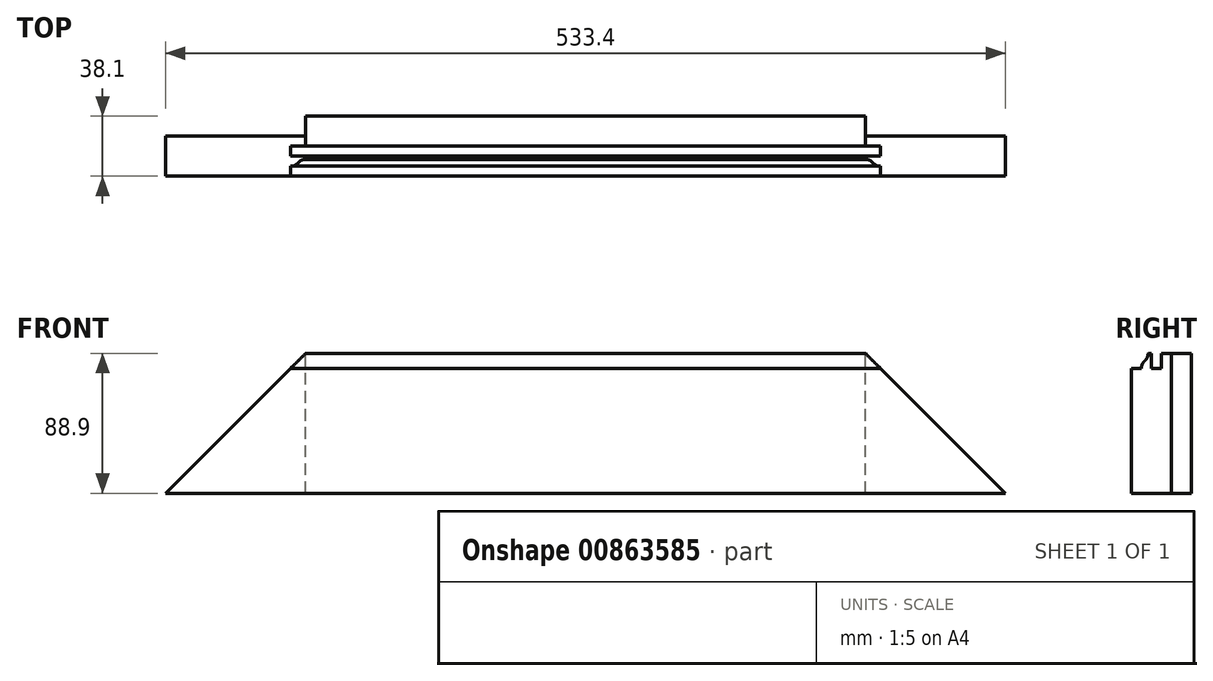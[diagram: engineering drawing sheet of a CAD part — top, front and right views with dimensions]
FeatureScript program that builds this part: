
annotation { "Feature Type Name" : "Feature", "Feature Type Description" : "" }
export const myFeature = defineFeature(function(context is Context, id is Id, definition is map)
    precondition{}
    {
        {
            var Q0;
            Q0=qCreatedBy(makeId("Front.planeOp"),FACE);
            var sketch = newSketch(context, id + "F0", { "sketchPlane" : qUnion([Q0])});
            skLineSegment(sketch, "E0.bottom", {"start": v(-266.7, 44.45) * mm, "end": v(266.7, 44.45) * mm});
            skLineSegment(sketch, "E0.top", {"start": v(-266.7, -44.45) * mm, "end": v(266.7, -44.45) * mm});
            skLineSegment(sketch, "E0.left", {"start": v(-266.7, 44.45) * mm, "end": v(-266.7, -44.45) * mm});
            skLineSegment(sketch, "E0.right", {"start": v(266.7, 44.45) * mm, "end": v(266.7, -44.45) * mm});
            skPoint(sketch, "E0.middle", {"position": v(0, 0) * mm});
            skSolve(sketch);
        }
        {
            var Q0;
            Q0=qSketchRegion(id+"F0",true);
            extrude(context, id + "F1", {"entities" : qUnion([Q0]), "oppositeDirection" : true, "depth" : 38.1 * mm, "offsetDistance" : 25.4 * mm});
        }
        {
            var Q0;
            Q0=makeQuery(id+"F1.opExtrude","SWEPT_FACE",FACE,{"disambiguationData":[OSD([sQuery(id+"F0.wireOp",EDGE,"E0.right")])]});
            var sketch = newSketch(context, id + "F2", { "sketchPlane" : qUnion([Q0])});
            skLineSegment(sketch, "E1", {"start": v(22.22, -38.1) * mm, "end": v(19.05, -44.45) * mm});
            skLineSegment(sketch, "E2", {"start": v(31.75, -44.45) * mm, "end": v(28.57, -38.1) * mm});
            skLineSegment(sketch, "E3", {"start": v(22.22, -38.1) * mm, "end": v(28.57, -38.1) * mm});
            skLineSegment(sketch, "E4", {"start": v(31.75, -44.45) * mm, "end": v(19.05, -44.45) * mm});
            skSolve(sketch);
        }
        {
            var Q0;
            Q0=makeQuery(id+"F1.opExtrude","SWEPT_FACE",FACE,{"disambiguationData":[OSD([sQuery(id+"F0.wireOp",EDGE,"E0.right")])]});
            var sketch = newSketch(context, id + "F3", { "sketchPlane" : qUnion([Q0])});
            skLineSegment(sketch, "E5", {"start": v(0, 34.93) * mm, "end": v(6.35, 34.93) * mm});
            skLineSegment(sketch, "E6", {"start": v(12.7, 34.93) * mm, "end": v(19.05, 34.93) * mm});
            skArc(sketch, "E7", {"start": v(8.5, 39.69) * mm, "mid": v(6.91, 37.54) * mm, "end": v(6.35, 34.93) * mm});
            skLineSegment(sketch, "E8", {"start": v(12.7, 44.45) * mm, "end": v(12.7, 34.93) * mm});
            skLineSegment(sketch, "E9", {"start": v(19.05, 34.93) * mm, "end": v(19.05, 44.45) * mm});
            skLineSegment(sketch, "E10", {"start": v(10.65, 44.45) * mm, "end": v(0, 44.45) * mm});
            skLineSegment(sketch, "E11", {"start": v(0, 44.45) * mm, "end": v(0, 34.93) * mm});
            skLineSegment(sketch, "E12", {"start": v(12.7, 44.45) * mm, "end": v(19.05, 44.45) * mm});
            skArc(sketch, "E13", {"start": v(8.5, 39.69) * mm, "mid": v(10.09, 41.84) * mm, "end": v(10.65, 44.45) * mm});
            skSolve(sketch);
        }
        {
            var Q0;
            Q0=qSketchRegion(id+"F3",true);
            extrude(context, id + "F4", {"entities" : qUnion([Q0]), "operationType" : NewBodyOperationType.REMOVE, "endBound" : BoundingType.THROUGH_ALL, "oppositeDirection" : true, "depth" : 25.4 * mm, "offsetDistance" : 25.4 * mm});
        }
        {
            var Q0;
            Q0=makeQuery(id+"F1.opExtrude","CAP_FACE",FACE,{"disambiguationData":[OSD([sQuery(id+"F0.wireOp",EDGE,"E0.bottom"),sQuery(id+"F0.wireOp",EDGE,"E0.top"),sQuery(id+"F0.wireOp",EDGE,"E0.left"),sQuery(id+"F0.wireOp",EDGE,"E0.right")])],"isStart":true});
            var sketch = newSketch(context, id + "F5", { "sketchPlane" : qUnion([Q0])});
            skLineSegment(sketch, "E14", {"start": v(-266.7, -44.45) * mm, "end": v(-177.8, 44.45) * mm});
            skLineSegment(sketch, "E15", {"start": v(-177.8, 44.45) * mm, "end": v(-266.7, 44.45) * mm});
            skLineSegment(sketch, "E16", {"start": v(-266.7, 44.45) * mm, "end": v(-266.7, -44.45) * mm});
            skPoint(sketch, "E17", {"position": v(-266.7, -4.76) * mm});
            skLineSegment(sketch, "E18", {"start": v(0, 760.27) * mm, "end": v(0, -577.9) * mm, "construction": true});
            skLineSegment(sketch, "E19.MirrorCS", {"start": v(266.7, 44.45) * mm, "end": v(266.7, -44.45) * mm});
            skLineSegment(sketch, "E20.MirrorCS", {"start": v(266.7, -44.45) * mm, "end": v(177.8, 44.45) * mm});
            skLineSegment(sketch, "E21.MirrorCS", {"start": v(177.8, 44.45) * mm, "end": v(266.7, 44.45) * mm});
            skSolve(sketch);
        }
        {
            var Q0;
            Q0=qSketchRegion(id+"F5",true);
            extrude(context, id + "F6", {"entities" : qUnion([Q0]), "operationType" : NewBodyOperationType.REMOVE, "oppositeDirection" : true, "depth" : 25.4 * mm, "offsetDistance" : 25.4 * mm});
        }
        {
            var Q0;
            {var subQ2=sQuery(id+"F0.wireOp",EDGE,"E0.bottom");Q0=makeQuery(id+"F4.boolean.opBoolean","SPLIT",FACE,{"disambiguationData":[TD([makeQuery(id+"F4.opExtrude","SWEPT_FACE",FACE,{"disambiguationData":[OSD([sQuery(id+"F3.wireOp",EDGE,"E9")])]})])],"derivedFrom":makeQuery(id+"F1.opExtrude","SWEPT_FACE",FACE,{"disambiguationData":[OSD([subQ2])]})});}
            var sketch = newSketch(context, id + "F7", { "sketchPlane" : qUnion([Q0])});
            skLineSegment(sketch, "E22.bottom", {"start": v(-266.7, 38.1) * mm, "end": v(-177.8, 38.1) * mm});
            skLineSegment(sketch, "E22.top", {"start": v(-266.7, 25.4) * mm, "end": v(-177.8, 25.4) * mm});
            skLineSegment(sketch, "E22.left", {"start": v(-266.7, 38.1) * mm, "end": v(-266.7, 25.4) * mm});
            skLineSegment(sketch, "E22.right", {"start": v(-177.8, 38.1) * mm, "end": v(-177.8, 25.4) * mm});
            skLineSegment(sketch, "E23", {"start": v(0, 107.05) * mm, "end": v(0, -115.05) * mm, "construction": true});
            skLineSegment(sketch, "E24.MirrorCS", {"start": v(266.7, 38.1) * mm, "end": v(177.8, 38.1) * mm});
            skLineSegment(sketch, "E25.MirrorCS", {"start": v(266.7, 38.1) * mm, "end": v(266.7, 25.4) * mm});
            skLineSegment(sketch, "E26.MirrorCS", {"start": v(266.7, 25.4) * mm, "end": v(177.8, 25.4) * mm});
            skLineSegment(sketch, "E27.MirrorCS", {"start": v(177.8, 38.1) * mm, "end": v(177.8, 25.4) * mm});
            skSolve(sketch);
        }
        {
            var Q0;
            Q0=qSketchRegion(id+"F7",true);
            extrude(context, id + "F8", {"entities" : qUnion([Q0]), "operationType" : NewBodyOperationType.REMOVE, "endBound" : BoundingType.UP_TO_NEXT, "oppositeDirection" : true, "depth" : 25.4 * mm, "offsetDistance" : 25.4 * mm});
        }
    });
